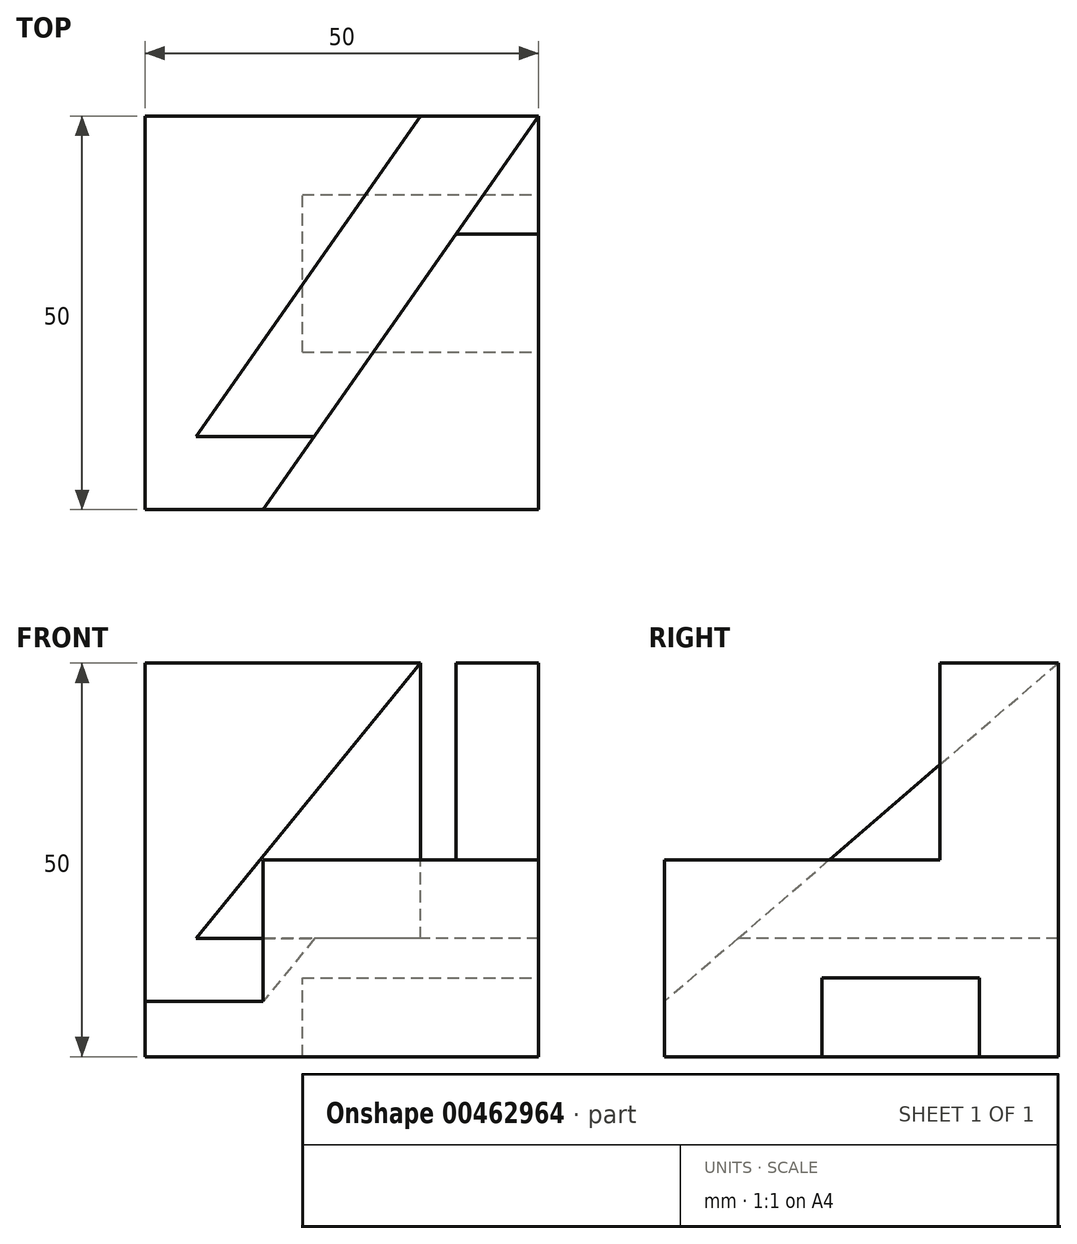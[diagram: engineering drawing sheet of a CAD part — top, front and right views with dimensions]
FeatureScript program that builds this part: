
annotation { "Feature Type Name" : "Feature", "Feature Type Description" : "" }
export const myFeature = defineFeature(function(context is Context, id is Id, definition is map)
    precondition{}
    {
        {
            var Q0;
            Q0=qCreatedBy(makeId("Right.planeOp"),FACE);
            var sketch = newSketch(context, id + "F0", { "sketchPlane" : qUnion([Q0])});
            skLineSegment(sketch, "E0.bottom", {"start": v(0, 0) * mm, "end": v(50, 0) * mm});
            skLineSegment(sketch, "E0.top", {"start": v(0, 50) * mm, "end": v(50, 50) * mm});
            skLineSegment(sketch, "E0.left", {"start": v(0, 0) * mm, "end": v(0, 50) * mm});
            skLineSegment(sketch, "E0.right", {"start": v(50, 0) * mm, "end": v(50, 50) * mm});
            skSolve(sketch);
        }
        {
            var Q0;
            Q0=makeQuery(id+"F0.imprint","IMPRINT",FACE,{"disambiguationData":[TD([[makeQuery(id+"F0.imprint","IMPRINT",EDGE,{"derivedFrom":sQuery(id+"F0.wireOp",EDGE,"E0.bottom")}),1.0]])]});
            extrude(context, id + "F1", {"entities" : qUnion([Q0]), "depth" : 50 * mm});
        }
        {
            var Q0;
            Q0=makeQuery(id+"F1.opExtrude","SWEPT_FACE",FACE,{"disambiguationData":[OSD([sQuery(id+"F0.wireOp",EDGE,"E0.top")])]});
            var sketch = newSketch(context, id + "F2", { "sketchPlane" : qUnion([Q0])});
            skLineSegment(sketch, "E1", {"start": v(50, 0) * mm, "end": v(15, 0) * mm});
            skLineSegment(sketch, "E2", {"start": v(50, 50) * mm, "end": v(15, 0) * mm});
            skLineSegment(sketch, "E3", {"start": v(50, 50) * mm, "end": v(35, 50) * mm});
            skLineSegment(sketch, "E4", {"start": v(35, 50) * mm, "end": v(0, 0) * mm});
            skLineSegment(sketch, "E5", {"start": v(0, 0) * mm, "end": v(15, 0) * mm});
            skSolve(sketch);
        }
        {
            var Q0;
            Q0=makeQuery(id+"F2.imprint","IMPRINT",FACE,{"disambiguationData":[TD([[makeQuery(id+"F2.imprint","IMPRINT",EDGE,{"derivedFrom":sQuery(id+"F2.wireOp",EDGE,"E2")}),-1.0]])]});
            extrude(context, id + "F3", {"entities" : qUnion([Q0]), "operationType" : NewBodyOperationType.REMOVE, "oppositeDirection" : true, "depth" : 35 * mm});
        }
        {
            var Q0;
            {var subQ0=sQuery(id+"F0.wireOp",EDGE,"E0.left");var subQ1=sQuery(id+"F0.wireOp",EDGE,"E0.top");Q0=makeQuery(id+"F3.boolean.opBoolean","SPLIT",FACE,{"disambiguationData":[TD([makeQuery(id+"F1.opExtrude","SWEPT_FACE",FACE,{"disambiguationData":[OSD([subQ0])]})])],"derivedFrom":makeQuery(id+"F1.opExtrude","SWEPT_FACE",FACE,{"disambiguationData":[OSD([subQ1])]})});}
            var sketch = newSketch(context, id + "F4", { "sketchPlane" : qUnion([Q0])});
            skLineSegment(sketch, "E6", {"start": v(50, 0) * mm, "end": v(50, 35) * mm});
            skLineSegment(sketch, "E7", {"start": v(50, 35) * mm, "end": v(39.5, 35) * mm});
            skSolve(sketch);
        }
        {
            var Q0;
            Q0=makeQuery(id+"F4.imprint","IMPRINT",FACE,{"disambiguationData":[TD([[makeQuery(id+"F4.imprint","IMPRINT",EDGE,{"derivedFrom":sQuery(id+"F4.wireOp",EDGE,"E6")}),1.0]])]});
            extrude(context, id + "F5", {"entities" : qUnion([Q0]), "operationType" : NewBodyOperationType.REMOVE, "oppositeDirection" : true, "depth" : 25 * mm});
        }
        {
            var Q0;
            Q0=makeQuery(id+"F1.opExtrude","CAP_FACE",FACE,{"disambiguationData":[OSD([sQuery(id+"F0.wireOp",EDGE,"E0.bottom"),sQuery(id+"F0.wireOp",EDGE,"E0.top"),sQuery(id+"F0.wireOp",EDGE,"E0.left"),sQuery(id+"F0.wireOp",EDGE,"E0.right")])],"isStart":true});
            var sketch = newSketch(context, id + "F6", { "sketchPlane" : qUnion([Q0])});
            skLineSegment(sketch, "E8", {"start": v(0, 0) * mm, "end": v(0, 7) * mm});
            skLineSegment(sketch, "E9", {"start": v(0, 7) * mm, "end": v(-50, 50) * mm});
            skLineSegment(sketch, "E10", {"start": v(-50, 50) * mm, "end": v(0, 50) * mm});
            skLineSegment(sketch, "E11", {"start": v(0, 50) * mm, "end": v(0, 7) * mm});
            skSolve(sketch);
        }
        {
            var Q0;
            {var subQ0=sQuery(id+"F6.wireOp",EDGE,"E9");Q0=makeQuery(id+"F6.imprint","IMPRINT",FACE,{"disambiguationData":[TD([[makeQuery(id+"F6.imprint","IMPRINT",EDGE,{"derivedFrom":subQ0}),-1.0]])]});}
            var Q1;
            Q1=makeQuery(id+"F3.boolean.opBoolean","COPY",FACE,{"derivedFrom":makeQuery(id+"F3.opExtrude","SWEPT_FACE",FACE,{"disambiguationData":[OSD([sQuery(id+"F2.wireOp",EDGE,"E2")])]})});
            extrude(context, id + "F7", {"entities" : qUnion([Q0]), "operationType" : NewBodyOperationType.REMOVE, "endBound" : BoundingType.UP_TO_SURFACE, "oppositeDirection" : true, "endBoundEntityFace" : qUnion([Q1]), "depth" : 25 * mm});
        }
        {
            var Q0;
            Q0=makeQuery(id+"F1.opExtrude","CAP_FACE",FACE,{"disambiguationData":[OSD([sQuery(id+"F0.wireOp",EDGE,"E0.bottom"),sQuery(id+"F0.wireOp",EDGE,"E0.top"),sQuery(id+"F0.wireOp",EDGE,"E0.left"),sQuery(id+"F0.wireOp",EDGE,"E0.right")])],"isStart":false});
            var sketch = newSketch(context, id + "F8", { "sketchPlane" : qUnion([Q0])});
            skLineSegment(sketch, "E12", {"start": v(0, 0) * mm, "end": v(20, 0) * mm});
            skLineSegment(sketch, "E13", {"start": v(20, 0) * mm, "end": v(40, 0) * mm});
            skLineSegment(sketch, "E14.top", {"start": v(20, 10) * mm, "end": v(40, 10) * mm});
            skLineSegment(sketch, "E14.left", {"start": v(20, 0) * mm, "end": v(20, 10) * mm});
            skLineSegment(sketch, "E14.right", {"start": v(40, 0) * mm, "end": v(40, 10) * mm});
            skSolve(sketch);
        }
        {
            var Q0;
            Q0 = qSketchRegion(id + "F8", true);
            extrude(context, id + "F9", {"entities" : qUnion([Q0]), "operationType" : NewBodyOperationType.REMOVE, "oppositeDirection" : true, "depth" : 30 * mm});
        }
    });
